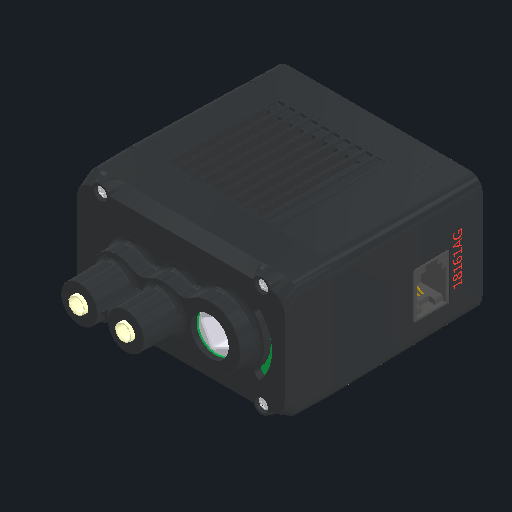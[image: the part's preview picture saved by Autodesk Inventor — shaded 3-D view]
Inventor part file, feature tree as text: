
AUTODESK INVENTOR PART (.ipt)
format: ipt  version: 2024 (Build 280153000, 153)  size: 8,699,392 bytes
history: native  units: in
note: dims shown in document units (in); Inventor stores cm internally (conversion verified against a paired STEP export)
features: other x15, extrude x2, sketch x2
ambient origin geometry x8: Origin, YZ Plane, XZ Plane, XY Plane, X Axis, Y Axis, Z Axis, Center Point
bodies: Solid1 (feature_tree), Solid2 (feature_tree), Solid4 (feature_tree), Solid6 (feature_tree), Solid7 (feature_tree), Solid8 (feature_tree), Solid9 (feature_tree), Solid14 (feature_tree), Solid16 (feature_tree), Solid17 (feature_tree), Solid18 (feature_tree), Solid19 (feature_tree), Solid20 (feature_tree), Solid21 (feature_tree), Solid22 (feature_tree)
feature tree (19):
  extrude  "Extrusion1"  TaperAngle=0.0deg  [1 undecoded]
  extrude  "Extrusion2"  Depth=0.1969in
  sketch  "Sketch1"  dims[d4=0.0in d5=0.0in]
  sketch  "Sketch2"  dims[d48=0.0197in d73=0.1969in d74=0.0148in d75=0.0591in d121=0.0984in d126=0.0394in d131=0.002in d132=0.0in d133=0.002in d134=0.0in]
  other  "276-4840-001 Rev38_1:1"
  other  "276-4840-005 Rev27_2:1"
  other  "276-4840-902 Rev2_24:1"
  other  "276-4840-004 Rev16_4:1"
  other  "276-4840-015 Rev7_5:1"
  other  "276-4840-015 Rev7_6:1"
  other  "276-4840-015 Rev7_7:1"
  other  "276-4840-003 Rev27_12:1"
  other  "276-4840-018 Rev6_18:1"
  other  "276-4840-059 Rev2_19:1"
  other  "276-4840-062 Rev1_20:1"
  other  "276-4840-062 Rev1_21:1"
  other  "276-4840-062 Rev1_22:1"
  other  "276-4840-043 Rev8_14:1"
  other  "276-4840-043 Rev8_15:1"
note: 1 required parameter value undecoded (feature->parameter linkage not recoverable at this tier; creation-order binding heuristic only, values carry confidence <= 0.55)
